FCSTD DOCUMENT  (FreeCAD 0.21R33668 +26 (Git))
Label: Assembly001
License: All rights reserved
LicenseURL: http://en.wikipedia.org/wiki/All_rights_reserved
objects: App::Link×4, PartDesign::CoordinateSystem×1, App::Part×1, App::FeaturePython×1
note: 1 computed .brp shape members not serialized (recipe doc carries the construction recipe); baked Part::Feature solids carry a one-line shape summary decoded from their .brp
EXTERNAL_REF file=Piece001.FCStd obj=Body

FEATURE [PartDesign::CoordinateSystem] LCS_0
  AttacherType = Attacher::AttachEngine3D
  MapMode = 2
  Support = -> [X_Axis]
FEATURE [App::Link] Corps
  LinkPlacement = pos=(3.8147e-06,-9.53674e-07,-4.76837e-07) rot=(0,0,1;0rad)
  LinkedObject = -> <external Piece001.FCStd>#Body
  Placement = pos=(3.8147e-06,-9.53674e-07,-4.76837e-07) rot=(0,0,1;0rad)
FEATURE [App::Link] Corps001
  LinkPlacement = pos=(10,-1.19209e-06,0) rot=(0,0,1;0rad)
  LinkedObject = -> <external Piece001.FCStd>#Body
  Placement = pos=(10,-1.19209e-06,0) rot=(0,0,1;0rad)
FEATURE [App::Link] Corps002
  LinkPlacement = pos=(20,-2.38419e-06,0) rot=(0,0,1;0rad)
  LinkedObject = -> <external Piece001.FCStd>#Body
  Placement = pos=(20,-2.38419e-06,0) rot=(0,0,1;0rad)
FEATURE [App::Link] Corps003
  LinkPlacement = pos=(30,-3.57628e-06,0) rot=(0,0,1;0rad)
  LinkedObject = -> <external Piece001.FCStd>#Body
  Placement = pos=(30,-3.57628e-06,0) rot=(0,0,1;0rad)
FEATURE [App::Part] Part001
  Group = -> [LCS_0,Corps,Corps001,Corps002,Corps003]
  Origin = -> Origin
FEATURE [App::FeaturePython] Variables  # WARN: FeaturePython — macro-defined, semantics opaque (R4)
  Type = App::PropertyContainer
  rotation_piece_1 = 10

RESOLVED EXTERNAL PARTS (link-assembly join: the EXTERNAL_REF files above that resolve inside this repo's crawl, each included once):
---- part Piece001.FCStd = doc fcstd_ea0c3290c417 ----
FCSTD DOCUMENT  (FreeCAD 0.21R33668 +26 (Git))
Label: Piece001
License: All rights reserved
LicenseURL: http://en.wikipedia.org/wiki/All_rights_reserved
objects: Sketcher::SketchObject×1, PartDesign::Pad×1, PartDesign::Body×1
note: 4 computed .brp shape members not serialized (recipe doc carries the construction recipe); baked Part::Feature solids carry a one-line shape summary decoded from their .brp

FEATURE [Sketcher::SketchObject] Sketch
  FullyConstrained = true
  MapMode = 5
  Placement = pos=(0,0,0) rot=(0.57735,0.57735,0.57735;2.0944rad)
  Support = -> [YZ_Plane]
  sketch-geometry (5):
    g0: LineSegment StartX=-5 StartY=-5 StartZ=0 EndX=45 EndY=-5 EndZ=0
    g1: LineSegment StartX=45 StartY=-5 StartZ=0 EndX=45 EndY=5 EndZ=0
    g2: LineSegment StartX=45 StartY=5 StartZ=0 EndX=-5 EndY=5 EndZ=0
    g3: LineSegment StartX=-5 StartY=5 StartZ=0 EndX=-5 EndY=-5 EndZ=0
    g4: Circle CenterX=0 CenterY=0 CenterZ=0 NormalX=0 NormalY=0 NormalZ=1 AngleXU=0 Radius=3
  constraints (14):
    c: Coincident(g0,g1)
    c: Coincident(g1,g2)
    c: Coincident(g2,g3)
    c: Coincident(g3,g0)
    c: Coincident(g4,g-1)
    c: Radius(g4) = 3
    c: Parallel(g2,g0)
    c: Parallel(g3,g1)
    c: Perpendicular(g1,g2)
    c: Distance(g4,g2) = 5
    c: Distance(g2,g1) = 50
    c: Distance(g1,g0) = 10
    c: Distance(g4,g3) = 5
    c: Angle(g-1,g2) = 0
FEATURE [PartDesign::Pad] Pad
  Direction = (1,-2e-16,3e-16)
  Length = 10
  Length2 = 10
  Placement = pos=(0,0,0) rot=(1,1,1;2.0944rad)
  Profile = -> Sketch
  ReferenceAxis = -> Sketch [N_Axis]
  Type = 0
FEATURE [PartDesign::Body] Body  label="Corps"
  Group = -> [Sketch,Pad]
  Origin = -> Origin
  Tip = -> Pad
